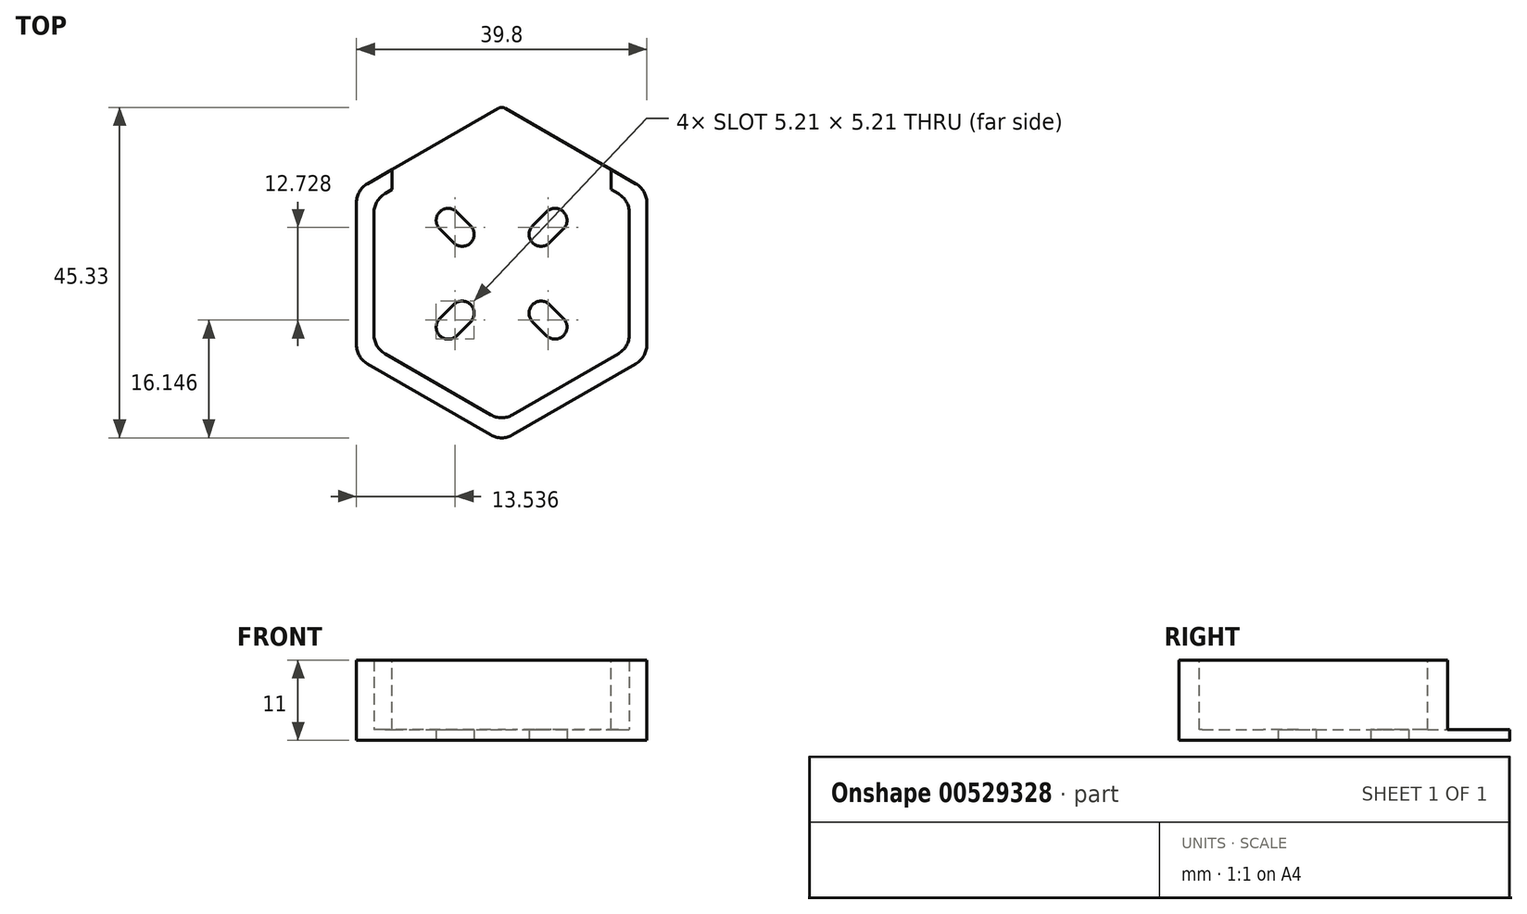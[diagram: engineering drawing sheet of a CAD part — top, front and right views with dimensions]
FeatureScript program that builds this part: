
annotation { "Feature Type Name" : "Feature", "Feature Type Description" : "" }
export const myFeature = defineFeature(function(context is Context, id is Id, definition is map)
    precondition{}
    {
        {
            var Q0;
            Q0=qCreatedBy(makeId("Top.planeOp"),FACE);
            var sketch = newSketch(context, id + "F0", { "sketchPlane" : qUnion([Q0])});
            skPoint(sketch, "E0", {"position": v(0, 0) * mm});
            skLineSegment(sketch, "E1", {"start": v(-20.56, -20.56) * mm, "end": v(20.56, 20.56) * mm, "construction": true});
            skLineSegment(sketch, "E2", {"start": v(-19.47, 19.47) * mm, "end": v(19.47, -19.47) * mm, "construction": true});
            skArc(sketch, "E3", {"start": v(-6.15, 8.49) * mm, "mid": v(-8.49, 8.49) * mm, "end": v(-8.49, 6.15) * mm});
            skArc(sketch, "E4", {"start": v(-6.58, 4.24) * mm, "mid": v(-4.24, 4.24) * mm, "end": v(-4.24, 6.58) * mm});
            skLineSegment(sketch, "E5", {"start": v(-6.15, 8.49) * mm, "end": v(-4.24, 6.58) * mm});
            skLineSegment(sketch, "E6", {"start": v(-8.49, 6.15) * mm, "end": v(-6.58, 4.24) * mm});
            skLineSegment(sketch, "E7.MirrorCS", {"start": v(-8.49, -6.15) * mm, "end": v(-6.58, -4.24) * mm});
            skArc(sketch, "E8.MirrorCS", {"start": v(-6.15, -8.49) * mm, "mid": v(-8.49, -8.49) * mm, "end": v(-8.49, -6.15) * mm});
            skArc(sketch, "E9.MirrorCS", {"start": v(-6.58, -4.24) * mm, "mid": v(-4.24, -4.24) * mm, "end": v(-4.24, -6.58) * mm});
            skLineSegment(sketch, "E10.MirrorCS", {"start": v(-6.15, -8.49) * mm, "end": v(-4.24, -6.58) * mm});
            skLineSegment(sketch, "E11.MirrorCS", {"start": v(6.15, -8.49) * mm, "end": v(4.24, -6.58) * mm});
            skLineSegment(sketch, "E12.MirrorCS", {"start": v(8.49, -6.15) * mm, "end": v(6.58, -4.24) * mm});
            skLineSegment(sketch, "E13.MirrorCS", {"start": v(6.15, 8.49) * mm, "end": v(4.24, 6.58) * mm});
            skArc(sketch, "E14.MirrorCS", {"start": v(6.58, -4.24) * mm, "mid": v(4.24, -4.24) * mm, "end": v(4.24, -6.58) * mm});
            skLineSegment(sketch, "E15.MirrorCS", {"start": v(8.49, 6.15) * mm, "end": v(6.58, 4.24) * mm});
            skArc(sketch, "E16.MirrorCS", {"start": v(6.15, -8.49) * mm, "mid": v(8.49, -8.49) * mm, "end": v(8.49, -6.15) * mm});
            skArc(sketch, "E17.MirrorCS", {"start": v(6.15, 8.49) * mm, "mid": v(8.49, 8.49) * mm, "end": v(8.49, 6.15) * mm});
            skArc(sketch, "E18.MirrorCS", {"start": v(6.58, 4.24) * mm, "mid": v(4.24, 4.24) * mm, "end": v(4.24, 6.58) * mm});
            skCircle(sketch, "E19.cCircle", {"center": v(0, 0) * mm, "radius": 17.5 * mm, "construction": true});
            skLineSegment(sketch, "E19.0", {"start": v(17.5, -10.1) * mm, "end": v(0, -20.2) * mm});
            skLineSegment(sketch, "E19.1", {"start": v(0, -20.2) * mm, "end": v(-17.5, -10.1) * mm});
            skLineSegment(sketch, "E19.2", {"start": v(-17.5, -10.1) * mm, "end": v(-17.5, 10.1) * mm});
            skLineSegment(sketch, "E19.3", {"start": v(-17.5, 10.1) * mm, "end": v(0, 20.2) * mm});
            skLineSegment(sketch, "E19.4", {"start": v(0, 20.2) * mm, "end": v(17.5, 10.1) * mm});
            skLineSegment(sketch, "E19.5", {"start": v(17.5, 10.1) * mm, "end": v(17.5, -10.1) * mm});
            skPoint(sketch, "E19.0.midPoint", {"position": v(8.75, -15.16) * mm});
            skLineSegment(sketch, "E20.0", {"start": v(-19.9, -11.49) * mm, "end": v(-19.9, 11.49) * mm});
            skLineSegment(sketch, "E20.1", {"start": v(0, 22.98) * mm, "end": v(19.9, 11.49) * mm});
            skLineSegment(sketch, "E20.2", {"start": v(19.9, 11.49) * mm, "end": v(19.9, -11.49) * mm});
            skLineSegment(sketch, "E20.3", {"start": v(-19.9, 11.49) * mm, "end": v(0, 22.98) * mm});
            skLineSegment(sketch, "E20.4", {"start": v(19.9, -11.49) * mm, "end": v(0, -22.98) * mm});
            skLineSegment(sketch, "E20.5", {"start": v(0, -22.98) * mm, "end": v(-19.9, -11.49) * mm});
            skSolve(sketch);
        }
        {
            var Q0;
            Q0=makeQuery(id+"F0.imprint","IMPRINT",FACE,{"disambiguationData":[TD([[makeQuery(id+"F0.imprint","IMPRINT",EDGE,{"derivedFrom":sQuery(id+"F0.wireOp",EDGE,"E3")}),-1.0]])]});
            extrude(context, id + "F1", {"entities" : qUnion([Q0]), "depth" : 1.5 * mm});
        }
        {
            var Q0;
            Q0=makeQuery(id+"F0.imprint","IMPRINT",FACE,{"disambiguationData":[TD([[makeQuery(id+"F0.imprint","IMPRINT",EDGE,{"derivedFrom":sQuery(id+"F0.wireOp",EDGE,"E19.0")}),1.0]])]});
            extrude(context, id + "F2", {"entities" : qUnion([Q0]), "operationType" : NewBodyOperationType.ADD, "depth" : 11 * mm});
        }
        {
            var Q0;
            Q0=qCreatedBy(makeId("Front.planeOp"),FACE);
            cPlane(context, id + "F3", {"entities" : qUnion([Q0]), "cplaneType" : CPlaneType.OFFSET, "offset" : 25 * mm, "oppositeDirection" : true, "width" : 150 * mm, "height" : 150 * mm});
        }
        {
            var Q0;
            Q0=qCreatedBy(id+"F3.planeOp",FACE);
            var sketch = newSketch(context, id + "F4", { "sketchPlane" : qUnion([Q0])});
            skLineSegment(sketch, "E21.bottom", {"start": v(-15, 1.5) * mm, "end": v(15, 1.5) * mm});
            skLineSegment(sketch, "E21.top", {"start": v(-15, 12.57) * mm, "end": v(15, 12.57) * mm});
            skLineSegment(sketch, "E21.left", {"start": v(-15, 1.5) * mm, "end": v(-15, 12.57) * mm});
            skLineSegment(sketch, "E21.right", {"start": v(15, 1.5) * mm, "end": v(15, 12.57) * mm});
            skPoint(sketch, "E21.middle", {"position": v(0, 7.04) * mm});
            skSolve(sketch);
        }
        {
            var Q0;
            Q0=makeQuery(id+"F4.imprint","IMPRINT",FACE,{"disambiguationData":[TD([[makeQuery(id+"F4.imprint","IMPRINT",EDGE,{"derivedFrom":sQuery(id+"F4.wireOp",EDGE,"E21.bottom")}),1.0]])]});
            extrude(context, id + "F5", {"entities" : qUnion([Q0]), "operationType" : NewBodyOperationType.REMOVE, "depth" : 26 * mm});
        }
        {
            var Q0;
            Q0=makeQuery(id+"F2.opExtrude","SWEPT_EDGE",EDGE,{"disambiguationData":[OSD([sQuery(id+"F0.wireOp",EDGE,"E20.1"),sQuery(id+"F0.wireOp",EDGE,"E20.2")])]});
            var Q1;
            Q1=makeQuery(id+"F2.opExtrude","SWEPT_EDGE",EDGE,{"disambiguationData":[OSD([sQuery(id+"F0.wireOp",EDGE,"E20.0"),sQuery(id+"F0.wireOp",EDGE,"E20.3")])]});
            var Q2;
            Q2=makeQuery(id+"F2.opExtrude","SWEPT_EDGE",EDGE,{"disambiguationData":[OSD([sQuery(id+"F0.wireOp",EDGE,"E20.0"),sQuery(id+"F0.wireOp",EDGE,"E20.5")])]});
            var Q3;
            Q3=makeQuery(id+"F2.opExtrude","SWEPT_EDGE",EDGE,{"disambiguationData":[OSD([sQuery(id+"F0.wireOp",EDGE,"E20.4"),sQuery(id+"F0.wireOp",EDGE,"E20.5")])]});
            var Q4;
            Q4=makeQuery(id+"F2.opExtrude","SWEPT_EDGE",EDGE,{"disambiguationData":[OSD([sQuery(id+"F0.wireOp",EDGE,"E20.2"),sQuery(id+"F0.wireOp",EDGE,"E20.4")])]});
            var Q5;
            Q5=makeQuery(id+"F2.opExtrude","SWEPT_EDGE",EDGE,{"disambiguationData":[OSD([sQuery(id+"F0.wireOp",EDGE,"E19.4"),sQuery(id+"F0.wireOp",EDGE,"E19.5")])]});
            var Q6;
            Q6=makeQuery(id+"F2.opExtrude","SWEPT_EDGE",EDGE,{"disambiguationData":[OSD([sQuery(id+"F0.wireOp",EDGE,"E19.0"),sQuery(id+"F0.wireOp",EDGE,"E19.5")])]});
            var Q7;
            Q7=makeQuery(id+"F2.opExtrude","SWEPT_EDGE",EDGE,{"disambiguationData":[OSD([sQuery(id+"F0.wireOp",EDGE,"E19.0"),sQuery(id+"F0.wireOp",EDGE,"E19.1")])]});
            var Q8;
            Q8=makeQuery(id+"F2.opExtrude","SWEPT_EDGE",EDGE,{"disambiguationData":[OSD([sQuery(id+"F0.wireOp",EDGE,"E19.1"),sQuery(id+"F0.wireOp",EDGE,"E19.2")])]});
            var Q9;
            Q9=makeQuery(id+"F2.opExtrude","SWEPT_EDGE",EDGE,{"disambiguationData":[OSD([sQuery(id+"F0.wireOp",EDGE,"E19.2"),sQuery(id+"F0.wireOp",EDGE,"E19.3")])]});
            fillet(context, id + "F6", {"entities" : qUnion([Q0, Q1, Q2, Q3, Q4, Q5, Q6, Q7, Q8, Q9]), "radius" : 3 * mm, "tangentPropagation" : true, "allowEdgeOverflow" : false});
        }
        {
            var Q0;
            Q0=makeQuery(id+"F1.opExtrude","CAP_EDGE",EDGE,{"disambiguationData":[OSD([sQuery(id+"F0.wireOp",EDGE,"E19.3")])],"isStart":false});
            var Q1;
            Q1=makeQuery(id+"F2.opExtrude","SWEPT_EDGE",EDGE,{"disambiguationData":[OSD([sQuery(id+"F0.wireOp",EDGE,"E20.1"),sQuery(id+"F0.wireOp",EDGE,"E20.3")])]});
            fillet(context, id + "F7", {"entities" : qUnion([Q0, Q1]), "radius" : 1 * mm, "tangentPropagation" : true, "allowEdgeOverflow" : false});
        }
    });
